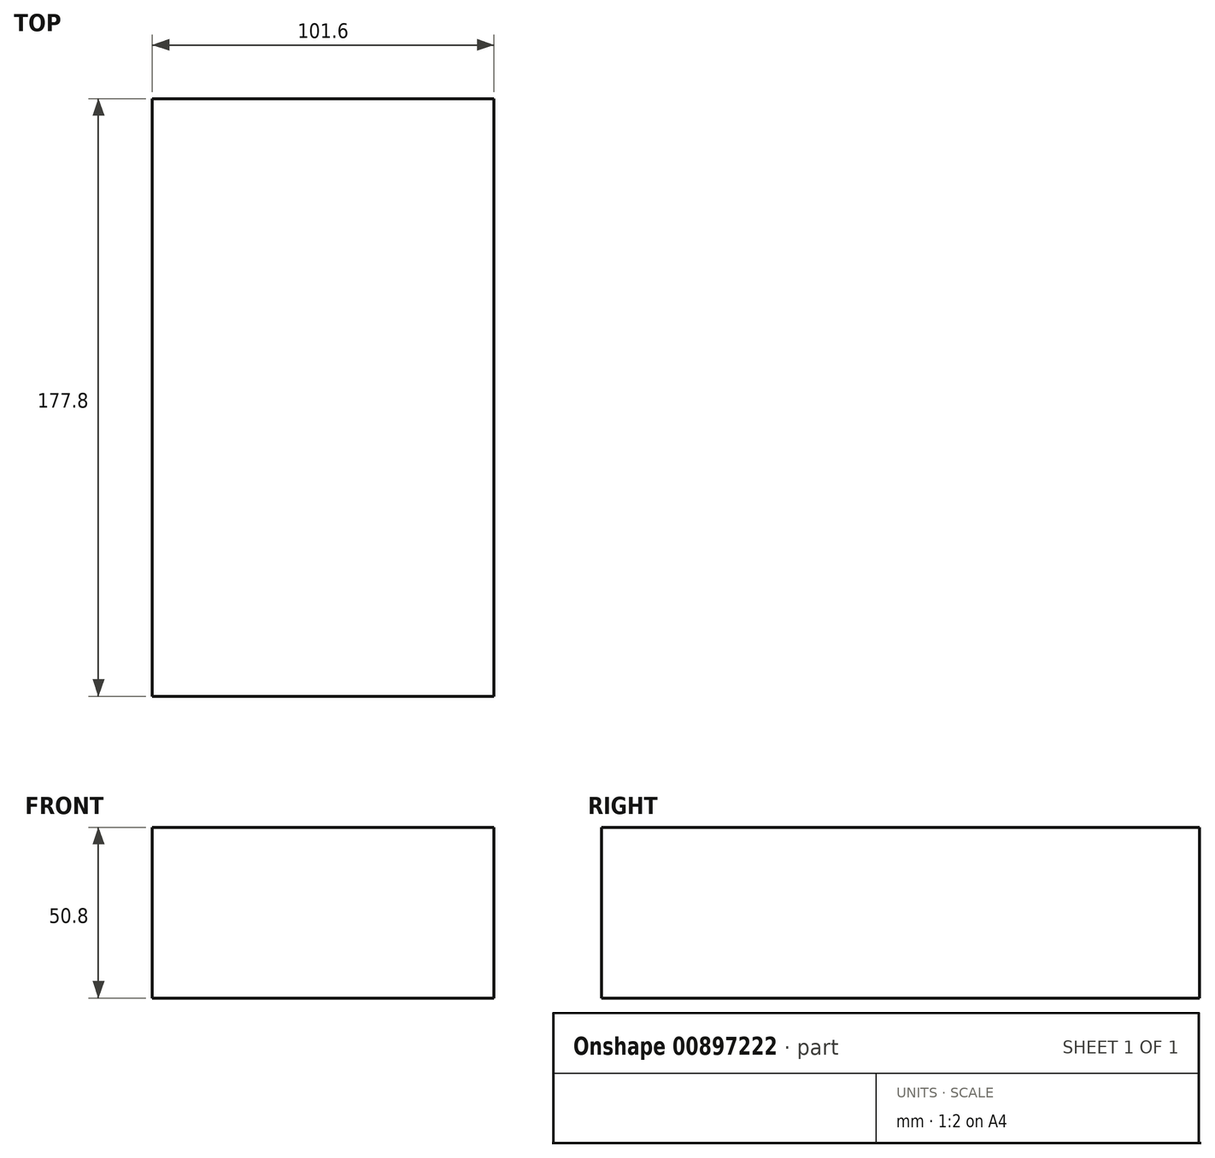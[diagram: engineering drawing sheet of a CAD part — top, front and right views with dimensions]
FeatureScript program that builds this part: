
annotation { "Feature Type Name" : "Feature", "Feature Type Description" : "" }
export const myFeature = defineFeature(function(context is Context, id is Id, definition is map)
    precondition{}
    {
        {
            var Q0;
            Q0=qCreatedBy(makeId("Top.planeOp"),FACE);
            var sketch = newSketch(context, id + "F0", { "sketchPlane" : qUnion([Q0])});
            skLineSegment(sketch, "E0.bottom", {"start": v(0, 0) * mm, "end": v(101.6, 0) * mm});
            skLineSegment(sketch, "E0.top", {"start": v(0, 177.8) * mm, "end": v(101.6, 177.8) * mm});
            skLineSegment(sketch, "E0.left", {"start": v(0, 0) * mm, "end": v(0, 177.8) * mm});
            skLineSegment(sketch, "E0.right", {"start": v(101.6, 0) * mm, "end": v(101.6, 177.8) * mm});
            skSolve(sketch);
        }
        {
            var Q0;
            Q0 = qSketchRegion(id + "F0", true);
            extrude(context, id + "F1", {"entities" : qUnion([Q0]), "oppositeDirection" : true, "depth" : 50.8 * mm, "offsetDistance" : 25.4 * mm});
        }
    });
